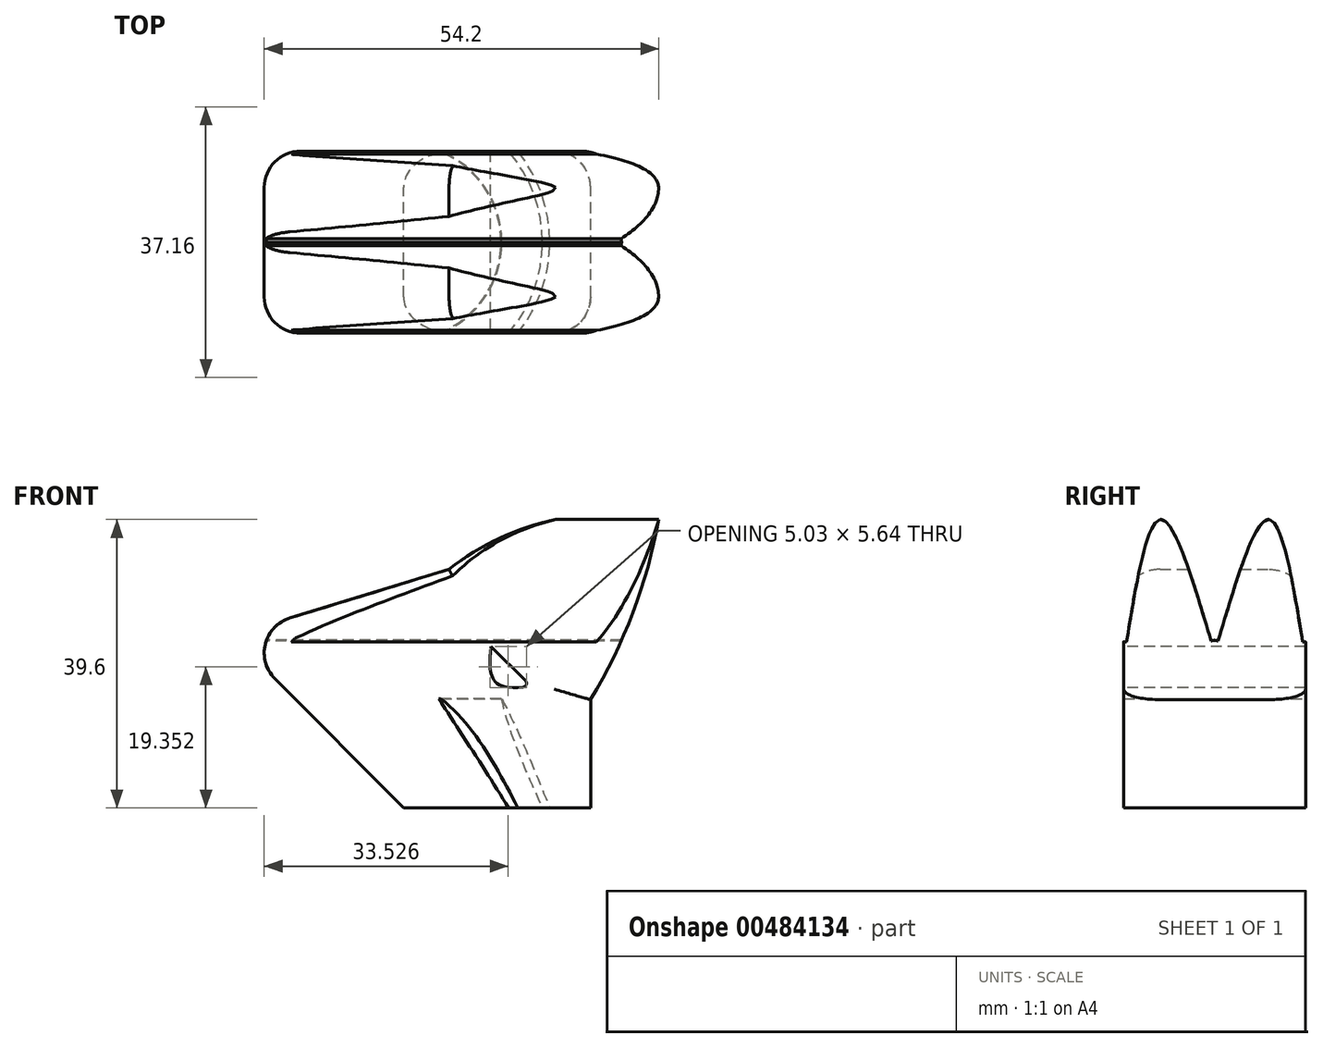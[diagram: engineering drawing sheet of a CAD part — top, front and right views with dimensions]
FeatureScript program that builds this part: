
annotation { "Feature Type Name" : "Feature", "Feature Type Description" : "" }
export const myFeature = defineFeature(function(context is Context, id is Id, definition is map)
    precondition{}
    {
        {
            var Q0;
            Q0=qCreatedBy(makeId("Front.planeOp"),FACE);
            var sketch = newSketch(context, id + "F0", { "sketchPlane" : qUnion([Q0])});
            skLineSegment(sketch, "E0.0", {"start": v(-15.3, 32.75) * mm, "end": v(-45.1, 23.64) * mm});
            skLineSegment(sketch, "E1.0", {"start": v(-45.1, 23.64) * mm, "end": v(-21.54, 0) * mm});
            skLineSegment(sketch, "E2.0", {"start": v(4.15, 0) * mm, "end": v(4.15, 14.86) * mm});
            skLineSegment(sketch, "E3", {"start": v(-21.54, 0) * mm, "end": v(4.15, 0) * mm});
            skLineSegment(sketch, "E4", {"start": v(6.95, 14.93) * mm, "end": v(22.6, 30.57) * mm});
            skLineSegment(sketch, "E5", {"start": v(6.95, 14.93) * mm, "end": v(23.08, 14.93) * mm, "construction": true});
            skArc(sketch, "E6", {"start": v(4.15, 14.86) * mm, "mid": v(9.97, 26.8) * mm, "end": v(13.51, 39.6) * mm});
            skArc(sketch, "E7", {"start": v(13.51, 39.6) * mm, "mid": v(-1.65, 39.36) * mm, "end": v(-15.3, 32.75) * mm});
            skSolve(sketch);
        }
        {
            var Q0;
            Q0 = qSketchRegion(id + "F0", true);
            extrude(context, id + "F1", {"entities" : qUnion([Q0]), "endBound" : BoundingType.SYMMETRIC, "depth" : 25 * mm});
        }
        {
            var Q0;
            Q0=makeQuery(id+"F1.opExtrude","SWEPT_FACE",FACE,{"disambiguationData":[OSD([sQuery(id+"F0.wireOp",EDGE,"E3")])]});
            var sketch = newSketch(context, id + "F2", { "sketchPlane" : qUnion([Q0])});
            skPoint(sketch, "E8.0.center.orphan", {"position": v(-21.54, 0) * mm});
            skLineSegment(sketch, "E9", {"start": v(-21.54, 12.5) * mm, "end": v(0, 12.5) * mm, "construction": true});
            skArc(sketch, "E10", {"start": v(-5.94, 12.5) * mm, "mid": v(-1.55, 0) * mm, "end": v(-5.94, -12.5) * mm});
            skArc(sketch, "E11.0", {"start": v(-6.28, 12.37) * mm, "mid": v(-1.9, -0.09) * mm, "end": v(-6.39, -12.5) * mm});
            skLineSegment(sketch, "E12", {"start": v(-5.94, -12.5) * mm, "end": v(-6.39, -12.5) * mm});
            skLineSegment(sketch, "E13", {"start": v(-5.94, 12.5) * mm, "end": v(-6.28, 12.37) * mm});
            skSolve(sketch);
        }
        {
            var Q0;
            Q0=qCreatedBy(makeId("Top.planeOp"),FACE);
            cPlane(context, id + "F3", {"entities" : qUnion([Q0]), "cplaneType" : CPlaneType.OFFSET, "offset" : 14 * mm, "width" : 150 * mm, "height" : 150 * mm});
        }
        {
            var Q0;
            Q0=makeQuery(id+"F1.opExtrude","CAP_EDGE",EDGE,{"disambiguationData":[OSD([sQuery(id+"F0.wireOp",EDGE,"E0.0")])],"isStart":false});
            var Q1;
            Q1=makeQuery(id+"F1.opExtrude","CAP_EDGE",EDGE,{"disambiguationData":[OSD([sQuery(id+"F0.wireOp",EDGE,"E7")])],"isStart":false});
            var Q2;
            Q2=makeQuery(id+"F1.opExtrude","CAP_EDGE",EDGE,{"disambiguationData":[OSD([sQuery(id+"F0.wireOp",EDGE,"E1.0")])],"isStart":false});
            var Q3;
            Q3=makeQuery(id+"F1.opExtrude","CAP_EDGE",EDGE,{"disambiguationData":[OSD([sQuery(id+"F0.wireOp",EDGE,"E6")])],"isStart":false});
            var Q4;
            Q4=makeQuery(id+"F1.opExtrude","CAP_EDGE",EDGE,{"disambiguationData":[OSD([sQuery(id+"F0.wireOp",EDGE,"E2.0")])],"isStart":false});
            var Q5;
            Q5=makeQuery(id+"F1.opExtrude","CAP_EDGE",EDGE,{"disambiguationData":[OSD([sQuery(id+"F0.wireOp",EDGE,"E2.0")])],"isStart":true});
            var Q6;
            Q6=makeQuery(id+"F1.opExtrude","CAP_EDGE",EDGE,{"disambiguationData":[OSD([sQuery(id+"F0.wireOp",EDGE,"E6")])],"isStart":true});
            var Q7;
            Q7=makeQuery(id+"F1.opExtrude","CAP_EDGE",EDGE,{"disambiguationData":[OSD([sQuery(id+"F0.wireOp",EDGE,"E7")])],"isStart":true});
            var Q8;
            Q8=makeQuery(id+"F1.opExtrude","CAP_EDGE",EDGE,{"disambiguationData":[OSD([sQuery(id+"F0.wireOp",EDGE,"E0.0")])],"isStart":true});
            var Q9;
            Q9=makeQuery(id+"F1.opExtrude","CAP_EDGE",EDGE,{"disambiguationData":[OSD([sQuery(id+"F0.wireOp",EDGE,"E1.0")])],"isStart":true});
            var Q10;
            Q10=makeQuery(id+"F1.opExtrude","SWEPT_EDGE",EDGE,{"disambiguationData":[OSD([sQuery(id+"F0.wireOp",EDGE,"E0.0"),sQuery(id+"F0.wireOp",EDGE,"E1.0")])]});
            fillet(context, id + "F4", {"entities" : qUnion([Q0, Q1, Q2, Q3, Q4, Q5, Q6, Q7, Q8, Q9, Q10]), "radius" : 5 * mm, "tangentPropagation" : true, "allowEdgeOverflow" : false});
        }
        {
            var Q0;
            Q0=qCreatedBy(makeId("Top.planeOp"),FACE);
            var sketch = newSketch(context, id + "F5", { "sketchPlane" : qUnion([Q0])});
            skPoint(sketch, "E14.0", {"position": v(-21.54, 0) * mm});
            skArc(sketch, "E15", {"start": v(-21.54, 20.07) * mm, "mid": v(-1.47, 0) * mm, "end": v(-21.54, -20.07) * mm});
            skArc(sketch, "E16.0", {"start": v(-21.54, 19.07) * mm, "mid": v(-2.47, 0) * mm, "end": v(-21.54, -19.07) * mm});
            skLineSegment(sketch, "E17", {"start": v(-21.54, 20.07) * mm, "end": v(-21.54, 19.07) * mm});
            skLineSegment(sketch, "E18", {"start": v(-21.54, -19.07) * mm, "end": v(-21.54, -20.07) * mm});
            skSolve(sketch);
        }
        {
            var Q0;
            Q0=qCreatedBy(id+"F3.planeOp",FACE);
            var sketch = newSketch(context, id + "F6", { "sketchPlane" : qUnion([Q0])});
            skArc(sketch, "E19", {"start": v(-21.54, 14) * mm, "mid": v(-7.54, 0) * mm, "end": v(-21.54, -14) * mm});
            skArc(sketch, "E20.0", {"start": v(-21.54, 13.65) * mm, "mid": v(-7.9, 0) * mm, "end": v(-21.54, -13.65) * mm});
            skLineSegment(sketch, "E21", {"start": v(-21.54, 14) * mm, "end": v(-21.54, 13.65) * mm});
            skLineSegment(sketch, "E22", {"start": v(-21.54, -13.65) * mm, "end": v(-21.54, -14) * mm});
            skSolve(sketch);
        }
        {
            var Q0;
            Q0=qCreatedBy(id+"F3.planeOp",FACE);
            cPlane(context, id + "F7", {"entities" : qUnion([Q0]), "cplaneType" : CPlaneType.OFFSET, "offset" : 1 * mm, "width" : 150 * mm, "height" : 150 * mm});
        }
        {
            var Q0;
            Q0=qCreatedBy(id+"F7.planeOp",FACE);
            var sketch = newSketch(context, id + "F8", { "sketchPlane" : qUnion([Q0])});
            skPoint(sketch, "E23.0", {"position": v(-21.54, 0) * mm});
            skArc(sketch, "E24", {"start": v(-21.54, -13.5) * mm, "mid": v(-8.04, 0) * mm, "end": v(-21.54, 13.5) * mm});
            skArc(sketch, "E25.0", {"start": v(-21.54, -13.4) * mm, "mid": v(-8.14, 0) * mm, "end": v(-21.54, 13.4) * mm});
            skLineSegment(sketch, "E26", {"start": v(-21.54, 13.5) * mm, "end": v(-21.54, 13.4) * mm});
            skLineSegment(sketch, "E27", {"start": v(-21.54, -13.4) * mm, "end": v(-21.54, -13.5) * mm});
            skSolve(sketch);
        }
        {
            var Q1;
            Q1 = qSketchRegion(id + "F5", true);
            var Q2;
            Q2 = qSketchRegion(id + "F6", true);
            var Q3;
            Q3 = qSketchRegion(id + "F8", true);
            loft(context, id + "F9", {"operationType" : NewBodyOperationType.REMOVE, "sheetProfilesArray" : [{ "sheetProfileEntities" : qUnion([Q1]) }, { "sheetProfileEntities" : qUnion([Q2]) }, { "sheetProfileEntities" : qUnion([Q3]) }]});
        }
        {
            var Q0;
            Q0=qCreatedBy(makeId("Front.planeOp"),FACE);
            var sketch = newSketch(context, id + "F10", { "sketchPlane" : qUnion([Q0])});
            skLineSegment(sketch, "E28", {"start": v(-4.8, 17.44) * mm, "end": v(-9.5, 22.17) * mm});
            skLineSegment(sketch, "E29", {"start": v(-4.1, 16.75) * mm, "end": v(-20, 16.75) * mm, "construction": true});
            skFitSpline(sketch, "E30", {"points": [v(-4.1, 16.75) * mm, v(-9.54, 18.56) * mm, v(-9.5, 22.17) * mm], "startDerivative": vector(-22.35, -4.06) * mm, "endDerivative": vector(1.01, 7.3) * mm});
            skArc(sketch, "E31.filletArc", {"start": v(-5.09, 16.6) * mm, "mid": v(-4.67, 16.93) * mm, "end": v(-4.8, 17.44) * mm});
            skSolve(sketch);
        }
        {
            var Q0;
            Q0 = qSketchRegion(id + "F10", true);
            extrude(context, id + "F11", {"entities" : qUnion([Q0]), "operationType" : NewBodyOperationType.REMOVE, "endBound" : BoundingType.SYMMETRIC, "oppositeDirection" : true, "depth" : 100 * mm});
        }
        {
            var Q0;
            Q0=qCreatedBy(makeId("Right.planeOp"),FACE);
            var sketch = newSketch(context, id + "F12", { "sketchPlane" : qUnion([Q0])});
            skLineSegment(sketch, "E32", {"start": v(0, 23.02) * mm, "end": v(0, 43.48) * mm, "construction": true});
            skLineSegment(sketch, "E33", {"start": v(-12.1, 22.76) * mm, "end": v(-12.6, 22.83) * mm});
            skLineSegment(sketch, "E34", {"start": v(-0.49, 22.91) * mm, "end": v(0, 23.02) * mm});
            skLineSegment(sketch, "E35.MirrorCS", {"start": v(0.49, 22.91) * mm, "end": v(0, 23.02) * mm});
            skLineSegment(sketch, "E36.MirrorCS", {"start": v(12.1, 22.76) * mm, "end": v(12.6, 22.83) * mm});
            skFitSpline(sketch, "E37", {"points": [v(-12.6, 22.83) * mm, v(-9.65, 51.35) * mm, v(0, 46.06) * mm], "startDerivative": vector(-48.02, 91.38) * mm, "endDerivative": vector(12.46, -54.58) * mm});
            skFitSpline(sketch, "E38.MirrorCS", {"points": [v(12.6, 22.83) * mm, v(9.65, 51.35) * mm, v(0, 46.06) * mm], "startDerivative": vector(48.02, 91.38) * mm, "endDerivative": vector(-12.46, -54.58) * mm});
            skFitSpline(sketch, "E39", {"points": [v(-12.1, 22.76) * mm, v(-7.43, 39.6) * mm, v(-0.49, 22.91) * mm], "startDerivative": vector(8.37, 50.58) * mm, "endDerivative": vector(14.85, -50) * mm});
            skFitSpline(sketch, "E40.MirrorCS", {"points": [v(12.1, 22.76) * mm, v(7.43, 39.6) * mm, v(0.49, 22.91) * mm], "startDerivative": vector(-8.37, 50.58) * mm, "endDerivative": vector(-14.85, -50) * mm});
            skSolve(sketch);
        }
        {
            var Q0;
            Q0 = qSketchRegion(id + "F12", true);
            extrude(context, id + "F13", {"entities" : qUnion([Q0]), "operationType" : NewBodyOperationType.REMOVE, "endBound" : BoundingType.SYMMETRIC, "depth" : 100 * mm});
        }
    });
